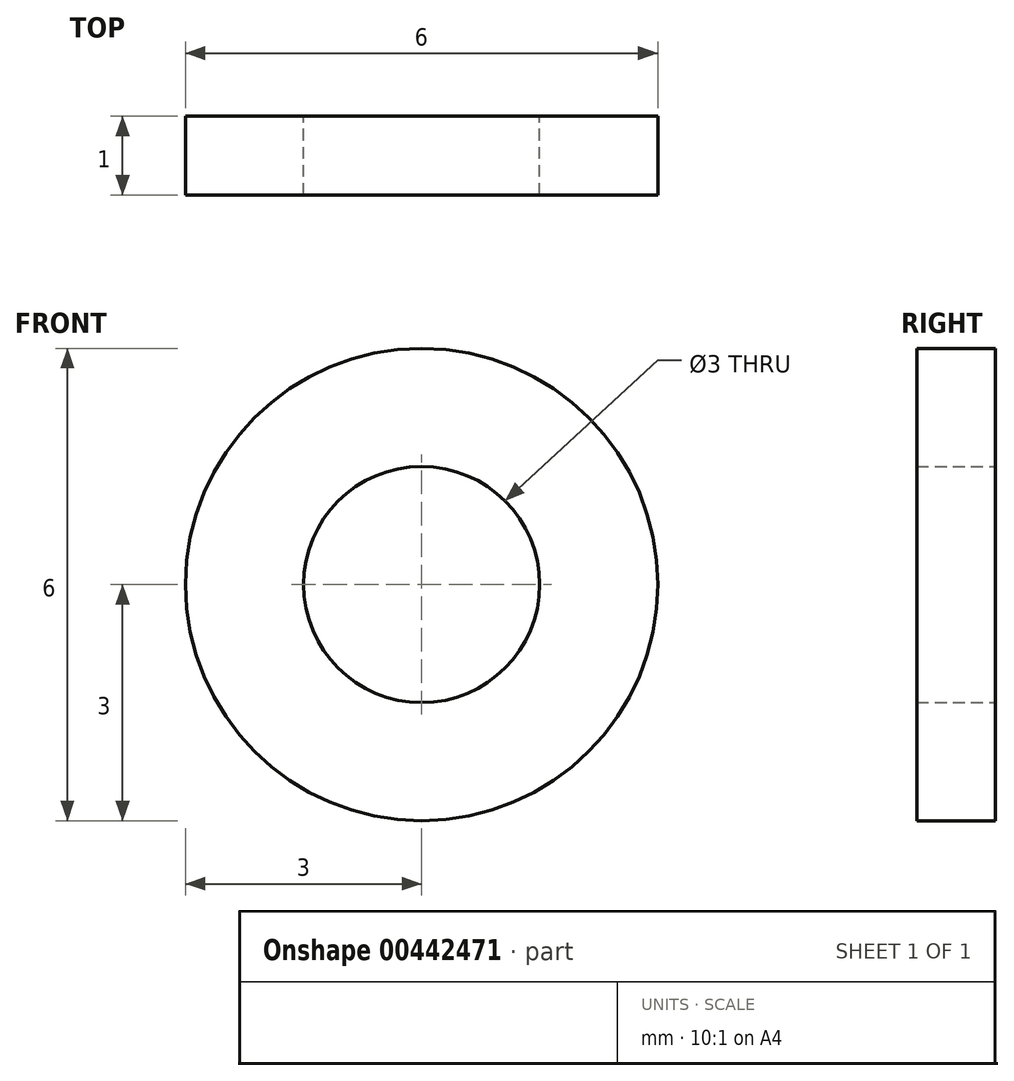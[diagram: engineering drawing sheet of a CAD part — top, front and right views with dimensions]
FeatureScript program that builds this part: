
annotation { "Feature Type Name" : "Feature", "Feature Type Description" : "" }
export const myFeature = defineFeature(function(context is Context, id is Id, definition is map)
    precondition{}
    {
        {
            var Q0;
            Q0=qCreatedBy(makeId("Front.planeOp"),FACE);
            var sketch = newSketch(context, id + "F0", { "sketchPlane" : qUnion([Q0])});
            skCircle(sketch, "E0", {"center": v(0, 0) * mm, "radius": 1.5 * mm});
            skCircle(sketch, "E1", {"center": v(0, 0) * mm, "radius": 3 * mm});
            skSolve(sketch);
        }
        {
            var Q0;
            Q0 = qSketchRegion(id + "F0", true);
            extrude(context, id + "F1", {"entities" : qUnion([Q0]), "depth" : 1 * mm});
        }
    });
